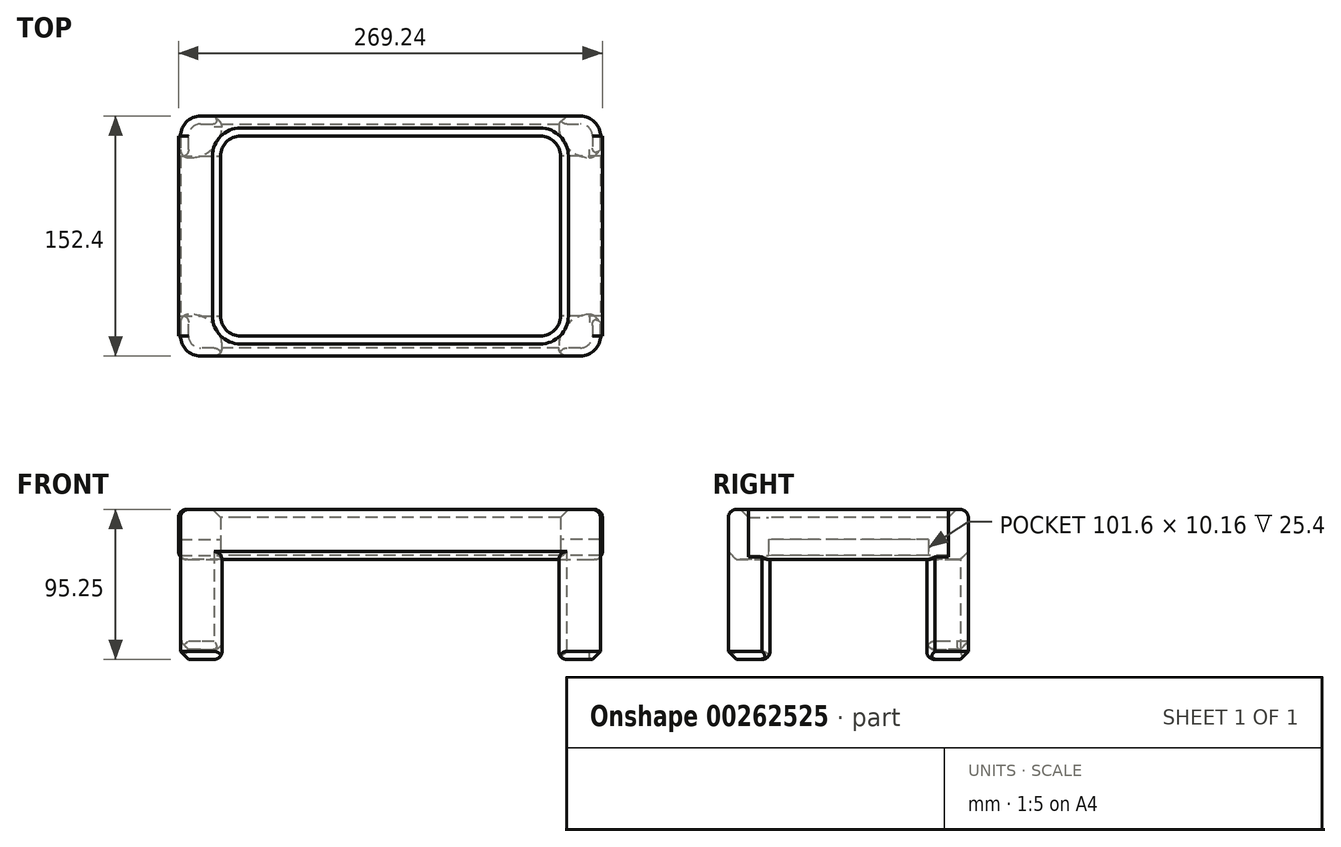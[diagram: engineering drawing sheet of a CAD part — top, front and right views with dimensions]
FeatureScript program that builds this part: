
annotation { "Feature Type Name" : "Feature", "Feature Type Description" : "" }
export const myFeature = defineFeature(function(context is Context, id is Id, definition is map)
    precondition{}
    {
        {
            var Q0;
            Q0=qCreatedBy(makeId("Top.planeOp"),FACE);
            var sketch = newSketch(context, id + "F0", { "sketchPlane" : qUnion([Q0])});
            skLineSegment(sketch, "E0.bottom", {"start": v(95.25, 63.5) * mm, "end": v(-95.25, 63.5) * mm});
            skLineSegment(sketch, "E0.top", {"start": v(95.25, -63.5) * mm, "end": v(-95.25, -63.5) * mm});
            skLineSegment(sketch, "E0.left", {"start": v(107.95, 50.8) * mm, "end": v(107.95, -50.8) * mm});
            skLineSegment(sketch, "E0.right", {"start": v(-107.95, 50.8) * mm, "end": v(-107.95, -50.8) * mm});
            skPoint(sketch, "E0.middle", {"position": v(0, 0) * mm});
            skLineSegment(sketch, "E1.bottom", {"start": v(120.65, 76.2) * mm, "end": v(-120.65, 76.2) * mm});
            skLineSegment(sketch, "E1.top", {"start": v(120.65, -76.2) * mm, "end": v(-120.65, -76.2) * mm});
            skLineSegment(sketch, "E1.left", {"start": v(133.35, 63.5) * mm, "end": v(133.35, -63.5) * mm});
            skLineSegment(sketch, "E1.right", {"start": v(-133.35, 63.5) * mm, "end": v(-133.35, -63.5) * mm});
            skPoint(sketch, "E2.visualSharp", {"position": v(-133.35, 76.2) * mm});
            skArc(sketch, "E2.filletArc", {"start": v(-120.65, 76.2) * mm, "mid": v(-129.63, 72.48) * mm, "end": v(-133.35, 63.5) * mm});
            skPoint(sketch, "E3.visualSharp", {"position": v(-133.35, -76.2) * mm});
            skArc(sketch, "E3.filletArc", {"start": v(-133.35, -63.5) * mm, "mid": v(-129.63, -72.48) * mm, "end": v(-120.65, -76.2) * mm});
            skPoint(sketch, "E4.visualSharp", {"position": v(133.35, -76.2) * mm});
            skArc(sketch, "E4.filletArc", {"start": v(120.65, -76.2) * mm, "mid": v(129.63, -72.48) * mm, "end": v(133.35, -63.5) * mm});
            skPoint(sketch, "E5.visualSharp", {"position": v(133.35, 76.2) * mm});
            skArc(sketch, "E5.filletArc", {"start": v(133.35, 63.5) * mm, "mid": v(129.63, 72.48) * mm, "end": v(120.65, 76.2) * mm});
            skPoint(sketch, "E6.visualSharp", {"position": v(107.95, 63.5) * mm});
            skArc(sketch, "E6.filletArc", {"start": v(107.95, 50.8) * mm, "mid": v(104.23, 59.78) * mm, "end": v(95.25, 63.5) * mm});
            skPoint(sketch, "E7.visualSharp", {"position": v(-107.95, 63.5) * mm});
            skArc(sketch, "E7.filletArc", {"start": v(-95.25, 63.5) * mm, "mid": v(-104.23, 59.78) * mm, "end": v(-107.95, 50.8) * mm});
            skPoint(sketch, "E8.visualSharp", {"position": v(-107.95, -63.5) * mm});
            skArc(sketch, "E8.filletArc", {"start": v(-107.95, -50.8) * mm, "mid": v(-104.23, -59.78) * mm, "end": v(-95.25, -63.5) * mm});
            skPoint(sketch, "E9.visualSharp", {"position": v(107.95, -63.5) * mm});
            skArc(sketch, "E9.filletArc", {"start": v(95.25, -63.5) * mm, "mid": v(104.23, -59.78) * mm, "end": v(107.95, -50.8) * mm});
            skPoint(sketch, "E10.endSnap0", {"position": v(129.63, 72.48) * mm});
            skArc(sketch, "E11", {"start": v(-107.95, -76.2) * mm, "mid": v(-112.8, -55.65) * mm, "end": v(-133.35, -50.8) * mm});
            skArc(sketch, "E12", {"start": v(133.35, -50.8) * mm, "mid": v(112.8, -55.65) * mm, "end": v(107.95, -76.2) * mm});
            skArc(sketch, "E13", {"start": v(107.95, 76.2) * mm, "mid": v(112.8, 55.65) * mm, "end": v(133.35, 50.8) * mm});
            skArc(sketch, "E14", {"start": v(-133.35, 50.8) * mm, "mid": v(-112.8, 55.65) * mm, "end": v(-107.95, 76.2) * mm});
            skSolve(sketch);
        }
        {
            var Q0;
            Q0=makeQuery(id+"F0.imprint","IMPRINT",FACE,{"disambiguationData":[TD([[makeQuery(id+"F0.imprint","IMPRINT",EDGE,{"derivedFrom":sQuery(id+"F0.wireOp",EDGE,"E0.bottom")}),1.0]])]});
            extrude(context, id + "F1", {"entities" : qUnion([Q0]), "depth" : 2.54 * mm});
        }
        {
            var Q0;
            Q0 = qSketchRegion(id + "F0", true);
            extrude(context, id + "F2", {"entities" : qUnion([Q0]), "operationType" : NewBodyOperationType.ADD, "depth" : 31.75 * mm});
        }
        {
            var Q0;
            {var subQ0=sQuery(id+"F0.wireOp",EDGE,"E3.filletArc");Q0=makeQuery(id+"F0.imprint","IMPRINT",FACE,{"disambiguationData":[TD([[makeQuery(id+"F0.imprint","IMPRINT",EDGE,{"derivedFrom":subQ0}),1.0]])]});}
            extrude(context, id + "F3", {"entities" : qUnion([Q0]), "operationType" : NewBodyOperationType.ADD, "oppositeDirection" : true, "depth" : 63.5 * mm});
        }
        {
            var Q0;
            {var subQ0=sQuery(id+"F0.wireOp",EDGE,"E4.filletArc");Q0=makeQuery(id+"F0.imprint","IMPRINT",FACE,{"disambiguationData":[TD([[makeQuery(id+"F0.imprint","IMPRINT",EDGE,{"derivedFrom":subQ0}),1.0]])]});}
            extrude(context, id + "F4", {"entities" : qUnion([Q0]), "operationType" : NewBodyOperationType.ADD, "oppositeDirection" : true, "depth" : 63.5 * mm});
        }
        {
            var Q0;
            {var subQ0=sQuery(id+"F0.wireOp",EDGE,"E5.filletArc");Q0=makeQuery(id+"F0.imprint","IMPRINT",FACE,{"disambiguationData":[TD([[makeQuery(id+"F0.imprint","IMPRINT",EDGE,{"derivedFrom":subQ0}),1.0]])]});}
            extrude(context, id + "F5", {"entities" : qUnion([Q0]), "operationType" : NewBodyOperationType.ADD, "oppositeDirection" : true, "depth" : 63.5 * mm});
        }
        {
            var Q0;
            {var subQ0=sQuery(id+"F0.wireOp",EDGE,"E2.filletArc");Q0=makeQuery(id+"F0.imprint","IMPRINT",FACE,{"disambiguationData":[TD([[makeQuery(id+"F0.imprint","IMPRINT",EDGE,{"derivedFrom":subQ0}),1.0]])]});}
            extrude(context, id + "F6", {"entities" : qUnion([Q0]), "operationType" : NewBodyOperationType.ADD, "oppositeDirection" : true, "depth" : 57.15 * mm});
        }
        {
            var Q0;
            Q0=makeQuery(id+"F2.opExtrude","SWEPT_FACE",FACE,{"disambiguationData":[OSD([sQuery(id+"F0.wireOp",EDGE,"E0.right")])]});
            var sketch = newSketch(context, id + "F7", { "sketchPlane" : qUnion([Q0])});
            skLineSegment(sketch, "E15.bottom", {"start": v(50.8, 2.54) * mm, "end": v(-50.8, 2.54) * mm});
            skLineSegment(sketch, "E15.top", {"start": v(50.8, 12.7) * mm, "end": v(-50.8, 12.7) * mm});
            skLineSegment(sketch, "E15.left", {"start": v(50.8, 2.54) * mm, "end": v(50.8, 12.7) * mm});
            skLineSegment(sketch, "E15.right", {"start": v(-50.8, 2.54) * mm, "end": v(-50.8, 12.7) * mm});
            skSolve(sketch);
        }
        {
            var Q0;
            Q0 = qSketchRegion(id + "F7", true);
            extrude(context, id + "F8", {"entities" : qUnion([Q0]), "operationType" : NewBodyOperationType.ADD, "oppositeDirection" : true, "depth" : 12.7 * mm});
        }
        {
            var Q0;
            Q0=makeQuery(id+"F7.imprint","IMPRINT",FACE,{"disambiguationData":[TD([[makeQuery(id+"F7.imprint","IMPRINT",EDGE,{"derivedFrom":sQuery(id+"F7.wireOp",EDGE,"E15.bottom")}),-1.0]])]});
            extrude(context, id + "F9", {"entities" : qUnion([Q0]), "operationType" : NewBodyOperationType.REMOVE, "oppositeDirection" : true, "depth" : 12.7 * mm});
        }
        {
            var Q0;
            Q0=makeQuery(id+"F7.imprint","IMPRINT",FACE,{"disambiguationData":[TD([[makeQuery(id+"F7.imprint","IMPRINT",EDGE,{"derivedFrom":sQuery(id+"F7.wireOp",EDGE,"E15.bottom")}),-1.0]])]});
            extrude(context, id + "F10", {"entities" : qUnion([Q0]), "operationType" : NewBodyOperationType.REMOVE, "oppositeDirection" : true, "depth" : 25.4 * mm});
        }
        {
            var Q0;
            Q0=makeQuery(id+"F2.opExtrude","SWEPT_FACE",FACE,{"disambiguationData":[OSD([sQuery(id+"F0.wireOp",EDGE,"E0.left")])]});
            var sketch = newSketch(context, id + "F11", { "sketchPlane" : qUnion([Q0])});
            skLineSegment(sketch, "E16.bottom", {"start": v(-50.8, 2.54) * mm, "end": v(50.8, 2.54) * mm});
            skLineSegment(sketch, "E16.top", {"start": v(-50.8, 12.7) * mm, "end": v(50.8, 12.7) * mm});
            skLineSegment(sketch, "E16.left", {"start": v(-50.8, 2.54) * mm, "end": v(-50.8, 12.7) * mm});
            skLineSegment(sketch, "E16.right", {"start": v(50.8, 2.54) * mm, "end": v(50.8, 12.7) * mm});
            skSolve(sketch);
        }
        {
            var Q0;
            Q0 = qSketchRegion(id + "F11", true);
            extrude(context, id + "F12", {"entities" : qUnion([Q0]), "operationType" : NewBodyOperationType.REMOVE, "oppositeDirection" : true, "depth" : 25.4 * mm});
        }
        {
            var Q0;
            {var subQ0=sQuery(id+"F0.wireOp",EDGE,"E1.right");Q0=makeQuery(id+"F6.boolean.opBoolean","MERGE",FACE,{"derivedFrom":[makeQuery(id+"F3.boolean.opBoolean","MERGE",FACE,{"derivedFrom":[makeQuery(id+"F2.opExtrude","SWEPT_FACE",FACE,{"disambiguationData":[OSD([subQ0])]}),makeQuery(id+"F3.opExtrude","SWEPT_FACE",FACE,{"disambiguationData":[OSD([subQ0])]})]}),makeQuery(id+"F6.opExtrude","SWEPT_FACE",FACE,{"disambiguationData":[OSD([subQ0])]})]});}
            var sketch = newSketch(context, id + "F13", { "sketchPlane" : qUnion([Q0])});
            skLineSegment(sketch, "E17.bottom", {"start": v(63.5, 31.75) * mm, "end": v(-63.5, 31.75) * mm});
            skLineSegment(sketch, "E17.top", {"start": v(63.5, 0) * mm, "end": v(-63.5, 0) * mm});
            skLineSegment(sketch, "E17.left", {"start": v(63.5, 31.75) * mm, "end": v(63.5, 0) * mm});
            skLineSegment(sketch, "E17.right", {"start": v(-63.5, 31.75) * mm, "end": v(-63.5, 0) * mm});
            skSolve(sketch);
        }
        {
            var Q0;
            Q0 = qSketchRegion(id + "F13", true);
            extrude(context, id + "F14", {"entities" : qUnion([Q0]), "operationType" : NewBodyOperationType.ADD, "depth" : 1.27 * mm});
        }
        {
            var Q0;
            {var subQ0=sQuery(id+"F0.wireOp",EDGE,"E1.left");Q0=makeQuery(id+"F5.boolean.opBoolean","MERGE",FACE,{"derivedFrom":[makeQuery(id+"F4.boolean.opBoolean","MERGE",FACE,{"derivedFrom":[makeQuery(id+"F2.opExtrude","SWEPT_FACE",FACE,{"disambiguationData":[OSD([subQ0])]}),makeQuery(id+"F4.opExtrude","SWEPT_FACE",FACE,{"disambiguationData":[OSD([subQ0])]})]}),makeQuery(id+"F5.opExtrude","SWEPT_FACE",FACE,{"disambiguationData":[OSD([subQ0])]})]});}
            var sketch = newSketch(context, id + "F15", { "sketchPlane" : qUnion([Q0])});
            skLineSegment(sketch, "E18.bottom", {"start": v(-63.5, 31.75) * mm, "end": v(63.5, 31.75) * mm});
            skLineSegment(sketch, "E18.top", {"start": v(-63.5, 0) * mm, "end": v(63.5, 0) * mm});
            skLineSegment(sketch, "E18.left", {"start": v(-63.5, 31.75) * mm, "end": v(-63.5, 0) * mm});
            skLineSegment(sketch, "E18.right", {"start": v(63.5, 31.75) * mm, "end": v(63.5, 0) * mm});
            skSolve(sketch);
        }
        {
            var Q0;
            Q0 = qSketchRegion(id + "F15", true);
            extrude(context, id + "F16", {"entities" : qUnion([Q0]), "operationType" : NewBodyOperationType.ADD, "depth" : 1.27 * mm});
        }
        {
            var Q0;
            Q0=makeQuery(id+"F2.opExtrude","CAP_EDGE",EDGE,{"disambiguationData":[OSD([sQuery(id+"F0.wireOp",EDGE,"E1.top")])],"isStart":false});
            fillet(context, id + "F17", {"entities" : qUnion([Q0]), "radius" : 5.08 * mm, "tangentPropagation" : true, "allowEdgeOverflow" : false});
        }
        {
            var Q0;
            Q0=makeQuery(id+"F2.opExtrude","CAP_EDGE",EDGE,{"disambiguationData":[OSD([sQuery(id+"F0.wireOp",EDGE,"E1.bottom")])],"isStart":false});
            fillet(context, id + "F18", {"entities" : qUnion([Q0]), "radius" : 5.08 * mm, "tangentPropagation" : true, "allowEdgeOverflow" : false});
        }
        {
            var Q0;
            Q0=makeQuery(id+"F16.opExtrude","CAP_EDGE",EDGE,{"disambiguationData":[OSD([sQuery(id+"F15.wireOp",EDGE,"E18.bottom")])],"isStart":false});
            fillet(context, id + "F19", {"entities" : qUnion([Q0]), "radius" : 5.08 * mm, "tangentPropagation" : true, "allowEdgeOverflow" : false});
        }
        {
            var Q0;
            Q0=makeQuery(id+"F14.opExtrude","CAP_EDGE",EDGE,{"disambiguationData":[OSD([sQuery(id+"F13.wireOp",EDGE,"E17.bottom")])],"isStart":false});
            fillet(context, id + "F20", {"entities" : qUnion([Q0]), "radius" : 5.08 * mm, "tangentPropagation" : true, "allowEdgeOverflow" : false});
        }
        {
            var Q0;
            Q0=makeQuery(id+"F2.opExtrude","CAP_EDGE",EDGE,{"disambiguationData":[OSD([sQuery(id+"F0.wireOp",EDGE,"E0.right")])],"isStart":false});
            chamfer(context, id + "F21", {"entities" : qUnion([Q0]), "width" : 5.08 * mm, "tangentPropagation" : true});
        }
        {
            var Q0;
            Q0=makeQuery(id+"F2.opExtrude","CAP_EDGE",EDGE,{"disambiguationData":[OSD([sQuery(id+"F0.wireOp",EDGE,"E1.top")])],"isStart":true});
            var Q1;
            Q1=makeQuery(id+"F4.opExtrude","CAP_EDGE",EDGE,{"disambiguationData":[OSD([sQuery(id+"F0.wireOp",EDGE,"E4.filletArc")])],"isStart":false});
            var Q2;
            Q2=makeQuery(id+"F3.opExtrude","CAP_EDGE",EDGE,{"disambiguationData":[OSD([sQuery(id+"F0.wireOp",EDGE,"E3.filletArc")])],"isStart":false});
            var Q3;
            Q3=makeQuery(id+"F6.opExtrude","CAP_EDGE",EDGE,{"disambiguationData":[OSD([sQuery(id+"F0.wireOp",EDGE,"E2.filletArc")])],"isStart":false});
            var Q4;
            {var subQ0=sQuery(id+"F0.wireOp",EDGE,"E1.bottom");Q4=makeQuery(id+"F6.boolean.opBoolean","MERGE",FACE,{"derivedFrom":[makeQuery(id+"F5.boolean.opBoolean","MERGE",FACE,{"derivedFrom":[makeQuery(id+"F2.opExtrude","SWEPT_FACE",FACE,{"disambiguationData":[OSD([subQ0])]}),makeQuery(id+"F5.opExtrude","SWEPT_FACE",FACE,{"disambiguationData":[OSD([subQ0])]})]}),makeQuery(id+"F6.opExtrude","SWEPT_FACE",FACE,{"disambiguationData":[OSD([subQ0])]})]});}
            chamfer(context, id + "F22", {"entities" : qUnion([Q0, Q1, Q2, Q3, Q4]), "width" : 5.08 * mm, "tangentPropagation" : true});
        }
        {
            var Q0;
            Q0=makeQuery(id+"F14.opExtrude","CAP_EDGE",EDGE,{"disambiguationData":[OSD([sQuery(id+"F13.wireOp",EDGE,"E17.top")])],"isStart":false});
            var Q1;
            Q1=makeQuery(id+"F16.opExtrude","CAP_EDGE",EDGE,{"disambiguationData":[OSD([sQuery(id+"F15.wireOp",EDGE,"E18.top")])],"isStart":false});
            fillet(context, id + "F23", {"entities" : qUnion([Q0, Q1]), "radius" : 5.08 * mm, "tangentPropagation" : true, "allowEdgeOverflow" : false});
        }
        {
            var Q0;
            Q0=makeQuery(id+"F4.opExtrude","SWEPT_EDGE",EDGE,{"disambiguationData":[OSD([sQuery(id+"F0.wireOp",EDGE,"E1.left"),sQuery(id+"F0.wireOp",EDGE,"E12")])]});
            var Q1;
            Q1=makeQuery(id+"F5.opExtrude","SWEPT_EDGE",EDGE,{"disambiguationData":[OSD([sQuery(id+"F0.wireOp",EDGE,"E1.left"),sQuery(id+"F0.wireOp",EDGE,"E13")])]});
            chamfer(context, id + "F24", {"entities" : qUnion([Q0, Q1]), "width" : 5.08 * mm, "tangentPropagation" : true});
        }
        {
            var Q0;
            Q0=makeQuery(id+"F4.opExtrude","CAP_EDGE",EDGE,{"disambiguationData":[OSD([sQuery(id+"F0.wireOp",EDGE,"E12")])],"isStart":false});
            var Q1;
            Q1=makeQuery(id+"F5.opExtrude","CAP_EDGE",EDGE,{"disambiguationData":[OSD([sQuery(id+"F0.wireOp",EDGE,"E13")])],"isStart":false});
            var Q2;
            Q2=makeQuery(id+"F3.opExtrude","CAP_EDGE",EDGE,{"disambiguationData":[OSD([sQuery(id+"F0.wireOp",EDGE,"E11")])],"isStart":false});
            var Q3;
            Q3=makeQuery(id+"F6.opExtrude","CAP_EDGE",EDGE,{"disambiguationData":[OSD([sQuery(id+"F0.wireOp",EDGE,"E14")])],"isStart":false});
            fillet(context, id + "F25", {"entities" : qUnion([Q0, Q1, Q2, Q3]), "radius" : 5.08 * mm, "tangentPropagation" : true, "allowEdgeOverflow" : false});
        }
        {
            var Q0;
            Q0=makeQuery(id+"F3.opExtrude","SWEPT_EDGE",EDGE,{"disambiguationData":[OSD([sQuery(id+"F0.wireOp",EDGE,"E1.top"),sQuery(id+"F0.wireOp",EDGE,"E11")])]});
            var Q1;
            Q1=makeQuery(id+"F4.opExtrude","SWEPT_EDGE",EDGE,{"disambiguationData":[OSD([sQuery(id+"F0.wireOp",EDGE,"E1.top"),sQuery(id+"F0.wireOp",EDGE,"E12")])]});
            var Q2;
            Q2=makeQuery(id+"F6.opExtrude","SWEPT_EDGE",EDGE,{"disambiguationData":[OSD([sQuery(id+"F0.wireOp",EDGE,"E1.right"),sQuery(id+"F0.wireOp",EDGE,"E14")])]});
            var Q3;
            {var subQ0=sQuery(id+"F0.wireOp",EDGE,"E13");Q3=makeQuery(id+"F24.opChamfer","BLEND_EDGE",EDGE,{"blendedFrom":[makeQuery(id+"F5.opExtrude","SWEPT_EDGE",EDGE,{"disambiguationData":[OSD([sQuery(id+"F0.wireOp",EDGE,"E1.left"),subQ0])]}),makeQuery(id+"F5.opExtrude","SWEPT_FACE",FACE,{"disambiguationData":[OSD([subQ0])]})],"blendedInto":[makeQuery(id+"F5.opExtrude","SWEPT_FACE",FACE,{"disambiguationData":[OSD([subQ0])]})]});}
            var Q4;
            {var subQ0=sQuery(id+"F0.wireOp",EDGE,"E12");Q4=makeQuery(id+"F24.opChamfer","BLEND_EDGE",EDGE,{"blendedFrom":[makeQuery(id+"F4.opExtrude","SWEPT_EDGE",EDGE,{"disambiguationData":[OSD([sQuery(id+"F0.wireOp",EDGE,"E1.left"),subQ0])]}),makeQuery(id+"F4.opExtrude","SWEPT_FACE",FACE,{"disambiguationData":[OSD([subQ0])]})],"blendedInto":[makeQuery(id+"F4.opExtrude","SWEPT_FACE",FACE,{"disambiguationData":[OSD([subQ0])]})]});}
            var Q5;
            Q5=makeQuery(id+"F3.opExtrude","SWEPT_EDGE",EDGE,{"disambiguationData":[OSD([sQuery(id+"F0.wireOp",EDGE,"E1.right"),sQuery(id+"F0.wireOp",EDGE,"E11")])]});
            var Q6;
            {var subQ0=sQuery(id+"F0.wireOp",EDGE,"E14");Q6=makeQuery(id+"F22.opChamfer","BLEND_EDGE",EDGE,{"blendedFrom":[makeQuery(id+"F6.opExtrude","SWEPT_EDGE",EDGE,{"disambiguationData":[OSD([sQuery(id+"F0.wireOp",EDGE,"E1.bottom"),subQ0])]}),makeQuery(id+"F6.opExtrude","SWEPT_FACE",FACE,{"disambiguationData":[OSD([subQ0])]})],"blendedInto":[makeQuery(id+"F6.opExtrude","SWEPT_FACE",FACE,{"disambiguationData":[OSD([subQ0])]})]});}
            fillet(context, id + "F26", {"entities" : qUnion([Q0, Q1, Q2, Q3, Q4, Q5, Q6]), "radius" : 5.08 * mm, "tangentPropagation" : true, "allowEdgeOverflow" : false});
        }
    });
